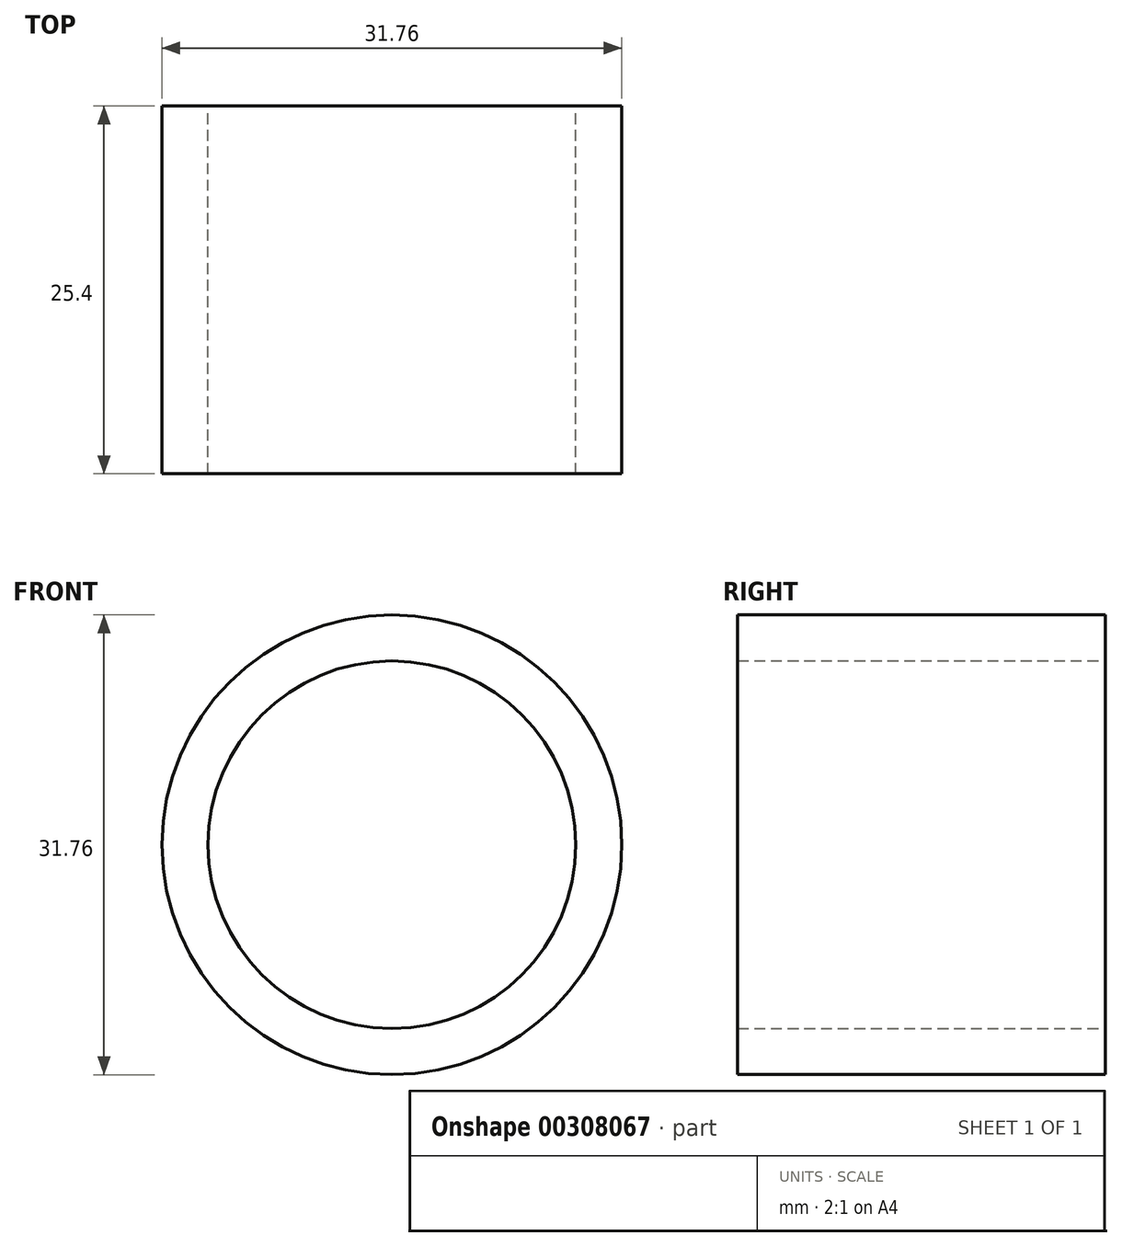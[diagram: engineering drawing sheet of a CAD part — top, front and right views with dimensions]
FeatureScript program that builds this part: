
annotation { "Feature Type Name" : "Feature", "Feature Type Description" : "" }
export const myFeature = defineFeature(function(context is Context, id is Id, definition is map)
    precondition{}
    {
        {
            var Q0;
            Q0=qCreatedBy(makeId("Front.planeOp"),FACE);
            var sketch = newSketch(context, id + "F0", { "sketchPlane" : qUnion([Q0])});
            skCircle(sketch, "E0", {"center": v(0, 0) * mm, "radius": 15.88 * mm});
            skCircle(sketch, "E1", {"center": v(0, 0) * mm, "radius": 12.7 * mm});
            skSolve(sketch);
        }
        {
            var Q0;
            Q0 = qSketchRegion(id + "F0", true);
            extrude(context, id + "F1", {"entities" : qUnion([Q0]), "depth" : 25.4 * mm, "offsetDistance" : 25.4 * mm});
        }
    });
